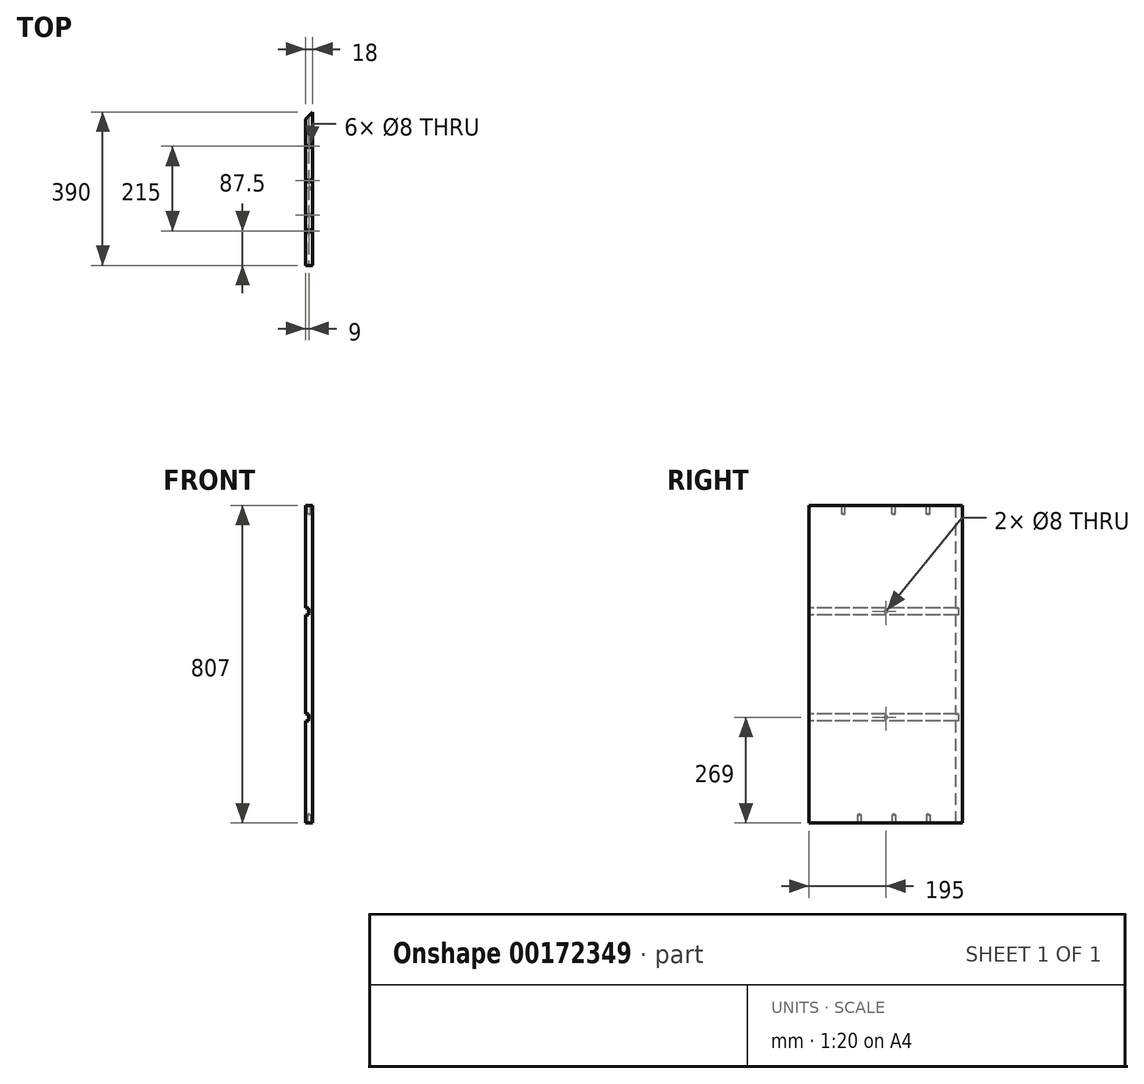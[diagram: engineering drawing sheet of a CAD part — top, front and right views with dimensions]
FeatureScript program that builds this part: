
annotation { "Feature Type Name" : "Feature", "Feature Type Description" : "" }
export const myFeature = defineFeature(function(context is Context, id is Id, definition is map)
    precondition{}
    {
        {
            var Q0;
            Q0=qCreatedBy(makeId("Right.planeOp"),FACE);
            var sketch = newSketch(context, id + "F0", { "sketchPlane" : qUnion([Q0])});
            skLineSegment(sketch, "E0.bottom", {"start": v(-195, 403.5) * mm, "end": v(195, 403.5) * mm});
            skLineSegment(sketch, "E0.top", {"start": v(-195, -403.5) * mm, "end": v(195, -403.5) * mm});
            skLineSegment(sketch, "E0.left", {"start": v(-195, 403.5) * mm, "end": v(-195, -403.5) * mm});
            skLineSegment(sketch, "E0.right", {"start": v(195, 403.5) * mm, "end": v(195, -403.5) * mm});
            skPoint(sketch, "E0.middle", {"position": v(0, 0) * mm});
            skPoint(sketch, "E1", {"position": v(0, -134.5) * mm});
            skPoint(sketch, "E2", {"position": v(0, 134.5) * mm});
            skLineSegment(sketch, "E3", {"start": v(195, 143.5) * mm, "end": v(-195, 143.5) * mm});
            skLineSegment(sketch, "E4", {"start": v(195, 125.5) * mm, "end": v(-195, 125.5) * mm});
            skLineSegment(sketch, "E5", {"start": v(195, -125.5) * mm, "end": v(-195, -125.5) * mm});
            skLineSegment(sketch, "E6", {"start": v(195, -143.5) * mm, "end": v(-195, -143.5) * mm});
            skSolve(sketch);
        }
        {
            var Q0;
            Q0=makeQuery(id+"F0.imprint","IMPRINT",FACE,{"disambiguationData":[TD([[makeQuery(id+"F0.imprint","IMPRINT",EDGE,{"derivedFrom":sQuery(id+"F0.wireOp",EDGE,"E0.bottom")}),-1.0]])]});
            var Q1;
            {var subQ0=sQuery(id+"F0.wireOp",EDGE,"E4");Q1=makeQuery(id+"F0.imprint","IMPRINT",FACE,{"disambiguationData":[TD([[makeQuery(id+"F0.imprint","IMPRINT",EDGE,{"derivedFrom":subQ0}),1.0]])]});}
            var Q2;
            {var subQ0=sQuery(id+"F0.wireOp",EDGE,"E0.top");Q2=makeQuery(id+"F0.imprint","IMPRINT",FACE,{"disambiguationData":[TD([[makeQuery(id+"F0.imprint","IMPRINT",EDGE,{"derivedFrom":subQ0}),1.0]])]});}
            var Q3;
            {var subQ0=sQuery(id+"F0.wireOp",EDGE,"E3");Q3=makeQuery(id+"F0.imprint","IMPRINT",FACE,{"disambiguationData":[TD([[makeQuery(id+"F0.imprint","IMPRINT",EDGE,{"derivedFrom":subQ0}),1.0]])]});}
            var Q4;
            {var subQ0=sQuery(id+"F0.wireOp",EDGE,"E5");Q4=makeQuery(id+"F0.imprint","IMPRINT",FACE,{"disambiguationData":[TD([[makeQuery(id+"F0.imprint","IMPRINT",EDGE,{"derivedFrom":subQ0}),1.0]])]});}
            extrude(context, id + "F1", {"entities" : qUnion([Q0, Q1, Q2, Q3, Q4]), "depth" : 18 * mm});
        }
        {
            var Q0;
            {var subQ0=sQuery(id+"F0.wireOp",EDGE,"E3");Q0=makeQuery(id+"F0.imprint","IMPRINT",FACE,{"disambiguationData":[TD([[makeQuery(id+"F0.imprint","IMPRINT",EDGE,{"derivedFrom":subQ0}),1.0]])]});}
            var Q1;
            {var subQ0=sQuery(id+"F0.wireOp",EDGE,"E5");Q1=makeQuery(id+"F0.imprint","IMPRINT",FACE,{"disambiguationData":[TD([[makeQuery(id+"F0.imprint","IMPRINT",EDGE,{"derivedFrom":subQ0}),1.0]])]});}
            extrude(context, id + "F2", {"entities" : qUnion([Q0, Q1]), "operationType" : NewBodyOperationType.REMOVE, "depth" : 8 * mm});
        }
        {
            var Q0;
            Q0=makeQuery(id+"F1.opExtrude","CAP_EDGE",EDGE,{"disambiguationData":[OSD([sQuery(id+"F0.wireOp",EDGE,"E0.right")])],"isStart":true});
            chamfer(context, id + "F3", {"entities" : qUnion([Q0]), "chamferType" : ChamferType.OFFSET_ANGLE, "width" : 18 * mm, "oppositeDirection" : false, "angle" : 45 * degree, "tangentPropagation" : true});
        }
        {
            var Q0;
            Q0=makeQuery(id+"F1.opExtrude","SWEPT_FACE",FACE,{"disambiguationData":[OSD([sQuery(id+"F0.wireOp",EDGE,"E0.bottom")])]});
            var sketch = newSketch(context, id + "F4", { "sketchPlane" : qUnion([Q0])});
            skPoint(sketch, "E7", {"position": v(9, 107.5) * mm});
            skPoint(sketch, "E8", {"position": v(9, -107.5) * mm});
            skPoint(sketch, "E9", {"position": v(9, 20) * mm});
            skLineSegment(sketch, "E10", {"start": v(0, 177) * mm, "end": v(18, 177) * mm});
            skSolve(sketch);
        }
        {
            var Q0;
            Q0=makeQuery(id+"F1.opExtrude","SWEPT_FACE",FACE,{"disambiguationData":[OSD([sQuery(id+"F0.wireOp",EDGE,"E0.top")])]});
            var sketch = newSketch(context, id + "F5", { "sketchPlane" : qUnion([Q0])});
            skPoint(sketch, "E11", {"position": v(9, -107.5) * mm});
            skPoint(sketch, "E12", {"position": v(9, -20) * mm});
            skPoint(sketch, "E13", {"position": v(9, 67.5) * mm});
            skSolve(sketch);
        }
        {
            var Q0;
            Q0=sQuery(id+"F4.wireOp",VERTEX,"E7");
            var Q1;
            Q1=sQuery(id+"F4.wireOp",VERTEX,"E9");
            var Q2;
            Q2=sQuery(id+"F4.wireOp",VERTEX,"E8");
            var Q3;
            Q3=sQuery(id+"F5.wireOp",VERTEX,"E11");
            var Q4;
            Q4=sQuery(id+"F5.wireOp",VERTEX,"E12");
            var Q5;
            Q5=sQuery(id+"F5.wireOp",VERTEX,"E13");
            var Q6;
            Q6=makeQuery(id+"F1.opExtrude","SWEPT_BODY",BODY,{"disambiguationData":[OSD([sQuery(id+"F0.wireOp",EDGE,"E0.bottom"),sQuery(id+"F0.wireOp",EDGE,"E0.top"),sQuery(id+"F0.wireOp",EDGE,"E0.left"),sQuery(id+"F0.wireOp",EDGE,"E0.right")])]});
            hole(context, id + "F6", {"style" : HoleStyle.SIMPLE, "endStyle" : HoleEndStyle.BLIND, "holeDiameter" : 8 * mm, "holeDepth" : 21 * mm, "startFromSketch" : true, "locations" : qUnion([Q0, Q1, Q2, Q3, Q4, Q5]), "scope" : qUnion([Q6])});
        }
        {
            var Q0;
            Q0=makeQuery(id+"F1.opExtrude","SWEPT_FACE",FACE,{"disambiguationData":[OSD([sQuery(id+"F0.wireOp",EDGE,"E0.bottom")])]});
            var sketch = newSketch(context, id + "F7", { "sketchPlane" : qUnion([Q0])});
            skCircle(sketch, "E14", {"center": v(18, 195) * mm, "radius": 320 * mm});
            skSolve(sketch);
        }
        {
            var Q0;
            Q0=sQuery(id+"F0.wireOp",VERTEX,"E1");
            var Q1;
            Q1=sQuery(id+"F0.wireOp",VERTEX,"E2");
            var Q2;
            Q2=makeQuery(id+"F1.opExtrude","SWEPT_BODY",BODY,{"disambiguationData":[OSD([sQuery(id+"F0.wireOp",EDGE,"E0.bottom"),sQuery(id+"F0.wireOp",EDGE,"E0.top"),sQuery(id+"F0.wireOp",EDGE,"E0.left"),sQuery(id+"F0.wireOp",EDGE,"E0.right")])]});
            hole(context, id + "F8", {"style" : HoleStyle.SIMPLE, "endStyle" : HoleEndStyle.BLIND, "oppositeDirection" : true, "holeDiameter" : 8 * mm, "holeDepth" : 11 * mm, "startFromSketch" : true, "locations" : qUnion([Q0, Q1]), "scope" : qUnion([Q2])});
        }
    });
